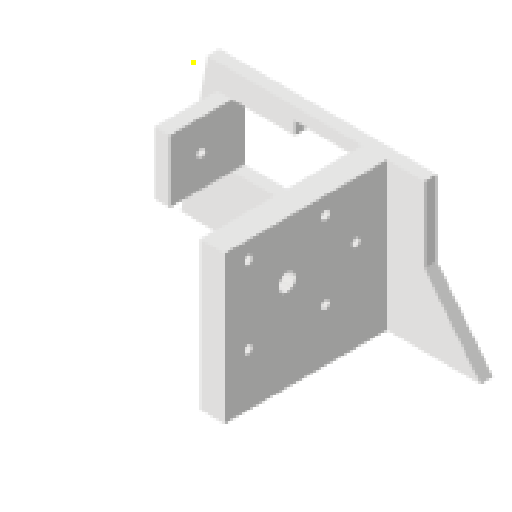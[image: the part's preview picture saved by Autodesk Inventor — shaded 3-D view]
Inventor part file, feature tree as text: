
AUTODESK INVENTOR PART (.ipt)
format: ipt  version: 2025.1 (Build 291241000, 241)  size: 215,552 bytes
history: native  units: mm
features: sketch x11, extrude x9, hole x3, other x1
ambient origin geometry x8: Origin, YZ Plane, XZ Plane, XY Plane, X Axis, Y Axis, Z Axis, Center Point
bodies: Body1 (feature_tree)
feature tree (24):
  other  "Bryła1"
  sketch  "Szkic1"
  extrude  "Wyciągnięcie proste1"  Depth=120.0mm
  extrude  "Wyciągnięcie proste2"  Depth=60.0mm
  extrude  "Wyciągnięcie proste3"  Depth=13.962634mm
  sketch  "Szkic2"
  extrude  "Wyciągnięcie proste4"  Depth=60.0mm
  extrude  "Wyciągnięcie proste5"  TaperAngle=0.0deg  [1 undecoded]
  extrude  "Wyciągnięcie proste6"  Depth=50.0mm
  hole  "Otwór1"  [1 undecoded]
  extrude  "Wyciągnięcie proste7"  Depth=10.0mm
  extrude  "Wyciągnięcie proste8"  Depth=10.0mm
  hole  "Otwór2"  [1 undecoded]
  hole  "Otwór3"  [1 undecoded]
  extrude  "Wyciągnięcie proste10"  Depth=5.0mm TaperAngle=0.0deg
  sketch  "Szkic3"
  sketch  "Szkic4"
  sketch  "Szkic5"
  sketch  "Szkic6"
  sketch  "Szkic7"
  sketch  "Szkic8"
  sketch  "Szkic9"
  sketch  "Szkic10"
  sketch  "Szkic12"
note: 4 required parameter values undecoded (feature->parameter linkage not recoverable at this tier; creation-order binding heuristic only, values carry confidence <= 0.55)
